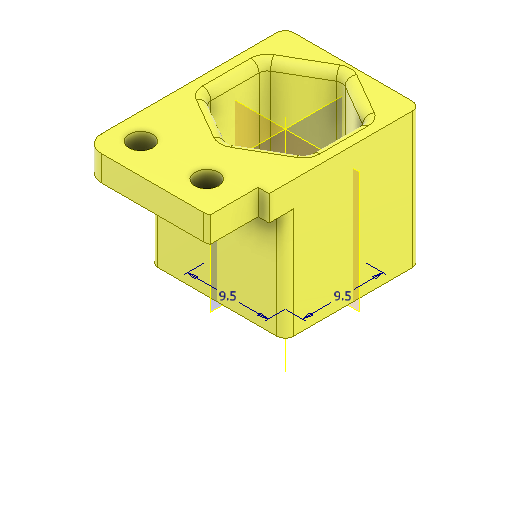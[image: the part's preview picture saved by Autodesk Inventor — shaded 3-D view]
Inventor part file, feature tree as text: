
AUTODESK INVENTOR PART (.ipt)
format: ipt  version: 2024.1 (Build 281209000, 209)  size: 249,856 bytes
history: native  units: mm
features: extrude x4, other x3, sketch x3, fillet x2, projected_geometry x2, plane x2, reference x1
ambient origin geometry x8: Origin, YZ Plane, XZ Plane, XY Plane, X Axis, Y Axis, Z Axis, Center Point
bodies: Volumenkörper1 (feature_tree)
feature tree (17):
  extrude  "Extrusion1"  Depth=16.0mm
  fillet  "Rundung1"  Radius=13.45mm
  extrude  "Extrusion2"  Depth=2.0mm
  fillet  "Rundung2"  Radius=11.85mm
  other  "Arbeitsachse1"
  extrude  "Extrusion3"  Depth=1.0mm
  extrude  "Extrusion4"  Depth=10.0mm
  sketch  "Skizze5"  dims[d7=13.0mm d8=0.0mm d9=1.0mm d10=10.0mm d11=2.8mm d12=2.8mm d13=2.0mm d14=3.0mm d15=0.0mm d16=0.1mm d17=0.0mm d18=0.0mm d19=9.5mm d20=9.5mm]
  sketch  "Skizze2"  dims[d0=16.0mm d1=16.0mm d2=13.45mm]
  projected_geometry  "Projizierte Kontur1"
  plane  "Arbeitsebene1"
  plane  "Arbeitsebene2"
  sketch  "Skizze3"  dims[d3=3.0mm d4=0.0mm d5=2.0mm d6=11.85mm]
  projected_geometry  "Projizierte Kontur2"
  reference  "Referenz1"
  other  "Assemlby_lightsheet_generator_passive_v2.iam"
  other  "30_Lightsheet_generator_passive_lid_v1:1"
